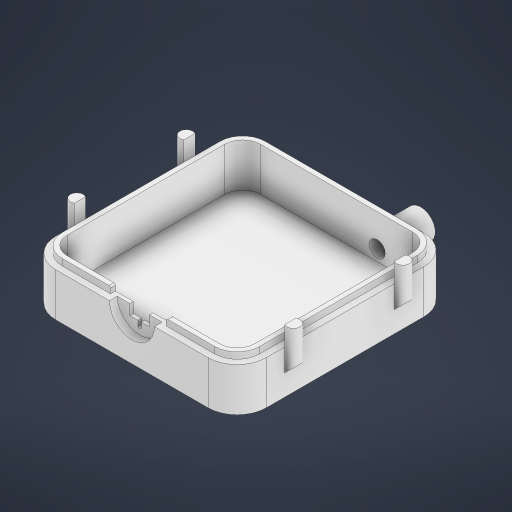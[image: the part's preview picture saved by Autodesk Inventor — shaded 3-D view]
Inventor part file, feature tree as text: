
AUTODESK INVENTOR PART (.ipt)
format: ipt  version: 2024 (Build 280153000, 153)  size: 403,456 bytes
history: native  units: in
note: dims shown in document units (in); Inventor stores cm internally (conversion verified against a paired STEP export)
features: sketch x7, extrude x7, fillet x3, mirror x2, hole x1, plane x1, chamfer x1
ambient origin geometry x8: Origin, YZ Plane, XZ Plane, XY Plane, X Axis, Y Axis, Z Axis, Center Point
bodies: Solid1 (feature_tree)
feature tree (22):
  sketch  "Sketch1"  dims[d3=0.3543in d4=0.3543in]
  extrude  "Extrusion1"  Depth=0.3543in
  extrude  "Extrusion2"  Depth=0.0787in TaperAngle=0.0deg
  extrude  "Extrusion3"  Depth=0.5315in
  extrude  "Extrusion4"  Depth=0.2559in
  extrude  "Extrusión11"  Depth=0.0197in
  fillet  "Empalme2"  Radius=0.0787in
  fillet  "Empalme3"  Radius=0.0787in
  hole  "Agujero1"  [1 undecoded]
  extrude  "Extrusión13"  Depth=0.0197in
  fillet  "Empalme8"  Radius=2.2953in
  plane  "Plano de trabajo1"
  extrude  "Extrusión14"  Depth=0.0197in
  mirror  "Simetría4"
  mirror  "Simetría5"
  chamfer  "Chaflán3"  Distance=0.7874in
  sketch  "Sketch2"  dims[d5=0.1378in d6=0.0787in d7=0.0in]
  sketch  "Sketch3"  dims[d8=0.5315in d9=0.0in d10=0.5512in]
  sketch  "Sketch11"  dims[d11=0.0945in d12=0.0in d13=0.2559in]
  sketch  "Boceto14"  dims[d15=0.0394in d17=0.0197in d18=0.0787in d19=0.0in d61=0.0787in]
  sketch  "Boceto15"  dims[d62=0.0787in d63=0.0787in d64=0.0in]
  sketch  "Boceto16"  dims[d65=0.0197in d66=0.0197in d75=2.2953in d76=2.3622in d82=0.7874in d83=0.315in d84=0.1969in d85=0.2362in d86=0.1575in d87=0.0787in d88=90.0deg d89=0.1378in d90=0.0in d91=0.2402in d92=0.3543in d93=0.3937in d94=0.0in d95=0.0787in d96=0.1969in d97=0.1969in d99=0.0394in d100=0.1575in d101=0.3937in d102=0.0in d106=0.1177in d107=0.0787in d108=45.0deg d44=0.0197in d45=0.0344in d46=0.0197in d47=0.0344in d51=0.0197in d52=0.0344in d53=0.0197in d54=0.0344in]
note: 1 required parameter value undecoded (feature->parameter linkage not recoverable at this tier; creation-order binding heuristic only, values carry confidence <= 0.55)
